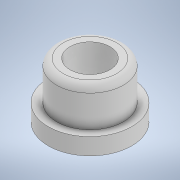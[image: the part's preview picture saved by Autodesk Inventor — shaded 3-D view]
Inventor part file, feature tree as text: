
AUTODESK INVENTOR PART (.ipt)
format: ipt  version: 2022 (Build 260153000, 153)  size: 133,120 bytes
history: native  units: mm
features: extrude x2, sketch x2, fillet x1
ambient origin geometry x8: Origin, YZ Plane, XZ Plane, XY Plane, X Axis, Y Axis, Z Axis, Center Point
bodies: Solid1 (feature_tree)
feature tree (5):
  extrude  "Extrusion1"  Depth=20.0mm
  extrude  "Extrusion2"  Depth=2.0mm
  fillet  "Fillet1"  Radius=5.0mm
  sketch  "Sketch1"  dims[d0=12.0mm d1=20.0mm]
  sketch  "Sketch2"  dims[d2=16.5mm d3=0.0mm d4=25.0mm d5=5.0mm d6=0.0mm d7=2.0mm d8=0.872665mm]
